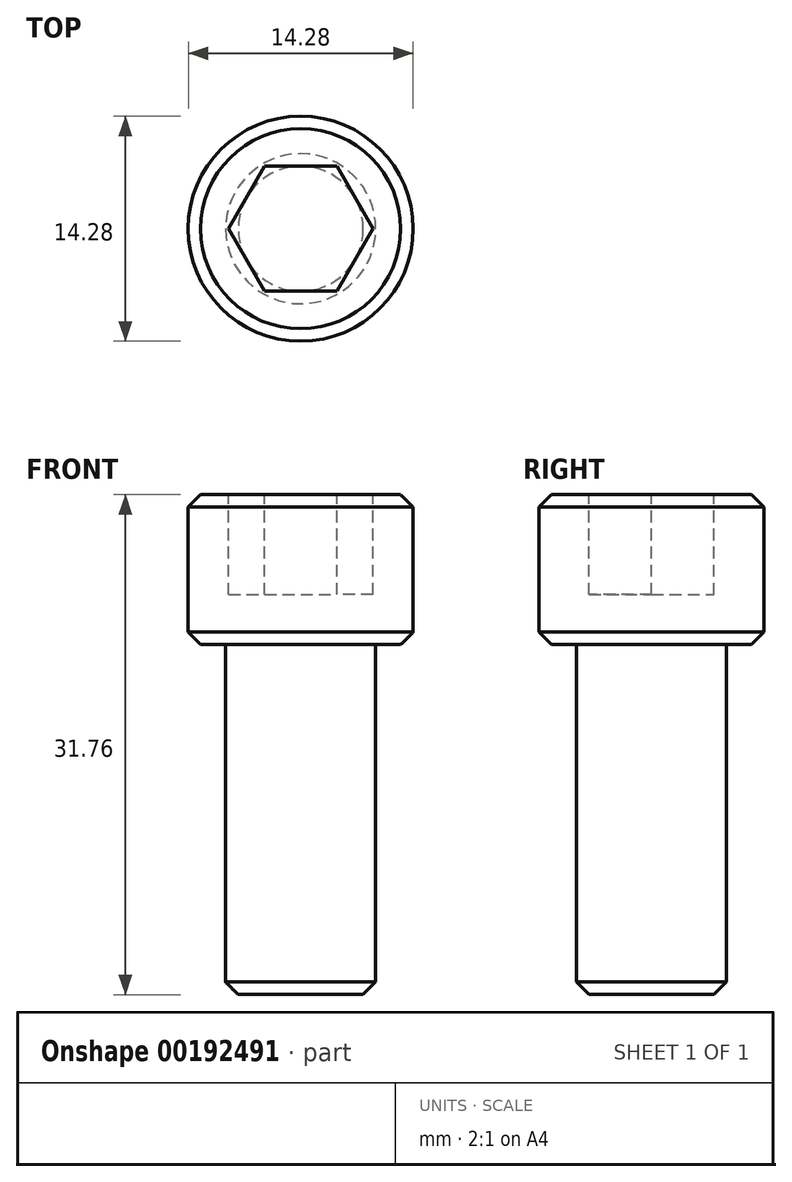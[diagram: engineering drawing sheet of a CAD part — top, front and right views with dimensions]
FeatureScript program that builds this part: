
annotation { "Feature Type Name" : "Feature", "Feature Type Description" : "" }
export const myFeature = defineFeature(function(context is Context, id is Id, definition is map)
    precondition{}
    {
        {
            var Q0;
            Q0=qCreatedBy(makeId("Top.planeOp"),FACE);
            var sketch = newSketch(context, id + "F0", { "sketchPlane" : qUnion([Q0])});
            skCircle(sketch, "E0", {"center": v(0, 0) * mm, "radius": 7.14 * mm});
            skSolve(sketch);
        }
        {
            var Q0;
            Q0 = qSketchRegion(id + "F0", true);
            extrude(context, id + "F1", {"entities" : qUnion([Q0]), "depth" : 9.52 * mm});
        }
        {
            var Q0;
            Q0=makeQuery(id+"F1.opExtrude","CAP_FACE",FACE,{"disambiguationData":[OSD([sQuery(id+"F0.wireOp",EDGE,"E0")])],"isStart":false});
            var sketch = newSketch(context, id + "F2", { "sketchPlane" : qUnion([Q0])});
            skCircle(sketch, "E1.cCircle", {"center": v(0, 0) * mm, "radius": 3.97 * mm, "construction": true});
            skLineSegment(sketch, "E1.0", {"start": v(-2.3, 3.97) * mm, "end": v(2.3, 3.97) * mm});
            skLineSegment(sketch, "E1.1", {"start": v(2.3, 3.97) * mm, "end": v(4.58, 0) * mm});
            skLineSegment(sketch, "E1.2", {"start": v(4.58, 0) * mm, "end": v(2.3, -3.97) * mm});
            skLineSegment(sketch, "E1.3", {"start": v(2.3, -3.97) * mm, "end": v(-2.3, -3.97) * mm});
            skLineSegment(sketch, "E1.4", {"start": v(-2.3, -3.97) * mm, "end": v(-4.58, 0) * mm});
            skLineSegment(sketch, "E1.5", {"start": v(-4.58, 0) * mm, "end": v(-2.3, 3.97) * mm});
            skPoint(sketch, "E1.0.midPoint", {"position": v(0, 3.97) * mm});
            skSolve(sketch);
        }
        {
            var Q0;
            Q0 = qSketchRegion(id + "F2", true);
            extrude(context, id + "F3", {"entities" : qUnion([Q0]), "operationType" : NewBodyOperationType.REMOVE, "oppositeDirection" : true, "depth" : 6.35 * mm});
        }
        {
            var Q0;
            Q0=makeQuery(id+"F1.opExtrude","CAP_FACE",FACE,{"disambiguationData":[OSD([sQuery(id+"F0.wireOp",EDGE,"E0")])],"isStart":true});
            var sketch = newSketch(context, id + "F4", { "sketchPlane" : qUnion([Q0])});
            skCircle(sketch, "E2", {"center": v(0, 0) * mm, "radius": 4.76 * mm});
            skSolve(sketch);
        }
        {
            var Q0;
            Q0 = qSketchRegion(id + "F4", true);
            extrude(context, id + "F5", {"entities" : qUnion([Q0]), "operationType" : NewBodyOperationType.ADD, "depth" : 22.22 * mm});
        }
        {
            var Q0;
            Q0=makeQuery(id+"F1.opExtrude","CAP_EDGE",EDGE,{"disambiguationData":[OSD([sQuery(id+"F0.wireOp",EDGE,"E0")])],"isStart":false});
            chamfer(context, id + "F6", {"entities" : qUnion([Q0]), "width" : 0.8 * mm, "tangentPropagation" : true});
        }
        {
            var Q0;
            Q0=makeQuery(id+"F1.opExtrude","CAP_EDGE",EDGE,{"disambiguationData":[OSD([sQuery(id+"F0.wireOp",EDGE,"E0")])],"isStart":true});
            chamfer(context, id + "F7", {"entities" : qUnion([Q0]), "width" : 0.8 * mm, "tangentPropagation" : true});
        }
        {
            var Q0;
            Q0=makeQuery(id+"F5.opExtrude","CAP_EDGE",EDGE,{"disambiguationData":[OSD([sQuery(id+"F4.wireOp",EDGE,"E2")])],"isStart":false});
            chamfer(context, id + "F8", {"entities" : qUnion([Q0]), "width" : 0.8 * mm, "tangentPropagation" : true});
        }
    });
